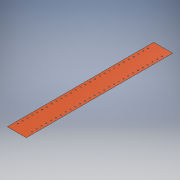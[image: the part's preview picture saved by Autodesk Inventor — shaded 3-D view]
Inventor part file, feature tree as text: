
AUTODESK INVENTOR PART (.ipt)
format: ipt  version: 2019 (Build 230136000, 136)  size: 219,136 bytes
history: native  units: mm
features: extrude x2, other x2, mirror x1
ambient origin geometry x8: Origin, YZ Plane, XZ Plane, XY Plane, X Axis, Y Axis, Z Axis, Center Point
bodies: Body1 (feature_tree)
feature tree (5):
  extrude  "Skin Body"  Depth=1405.0mm
  extrude  "End Cut"  Depth=702.5mm
  mirror  "End Cut Mirror"
  other  "Skin Scheme"
  other  "End Cut Outline"
